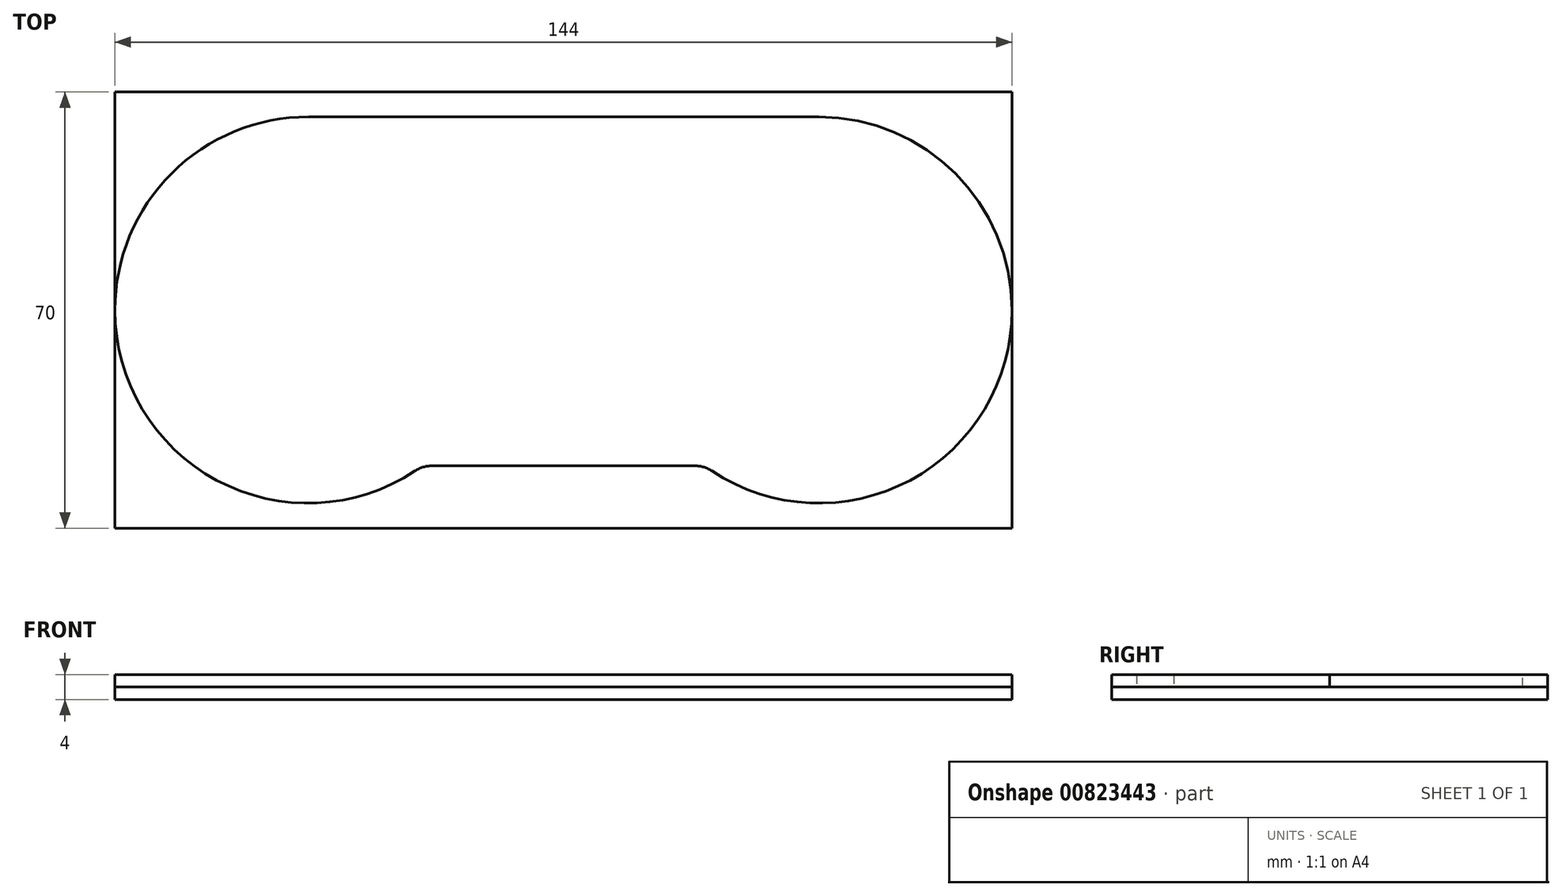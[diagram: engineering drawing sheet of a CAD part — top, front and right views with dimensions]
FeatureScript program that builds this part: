
annotation { "Feature Type Name" : "Feature", "Feature Type Description" : "" }
export const myFeature = defineFeature(function(context is Context, id is Id, definition is map)
    precondition{}
    {
        {
            var Q0;
            Q0=qCreatedBy(makeId("Top.planeOp"),FACE);
            var sketch = newSketch(context, id + "F0", { "sketchPlane" : qUnion([Q0])});
            skLineSegment(sketch, "E0.bottom", {"start": v(72, 35) * mm, "end": v(-72, 35) * mm});
            skLineSegment(sketch, "E0.top", {"start": v(72, -35) * mm, "end": v(-72, -35) * mm});
            skLineSegment(sketch, "E0.left", {"start": v(72, 35) * mm, "end": v(72, -35) * mm});
            skLineSegment(sketch, "E0.right", {"start": v(-72, 35) * mm, "end": v(-72, -35) * mm});
            skPoint(sketch, "E0.middle", {"position": v(0, 0) * mm});
            skArc(sketch, "E1", {"start": v(-40.92, 31) * mm, "mid": v(-70.7, -8.91) * mm, "end": v(-23.86, -25.83) * mm});
            skArc(sketch, "E2", {"start": v(23.86, -25.83) * mm, "mid": v(70.68, -8.95) * mm, "end": v(41, 31) * mm});
            skLineSegment(sketch, "E3", {"start": v(-40.92, 31) * mm, "end": v(41, 31) * mm});
            skPoint(sketch, "E4.visualSharp", {"position": v(-20.14, -22.93) * mm});
            skPoint(sketch, "E5.visualSharp", {"position": v(20.15, -22.94) * mm});
            skLineSegment(sketch, "E6.0", {"start": v(21.1, -25) * mm, "end": v(-21.1, -25) * mm});
            skPoint(sketch, "E7.start.orphan", {"position": v(41, -31) * mm});
            skPoint(sketch, "E8.visualSharp", {"position": v(22.67, -25) * mm});
            skArc(sketch, "E8.filletArc", {"start": v(23.86, -25.83) * mm, "mid": v(22.54, -25.21) * mm, "end": v(21.1, -25) * mm});
            skPoint(sketch, "E9.visualSharp", {"position": v(-22.67, -25) * mm});
            skArc(sketch, "E9.filletArc", {"start": v(-21.1, -25) * mm, "mid": v(-22.54, -25.21) * mm, "end": v(-23.86, -25.83) * mm});
            skSolve(sketch);
        }
        {
            var Q0;
            {var subQ4=sQuery(id+"F0.wireOp",EDGE,"E0.top");Q0=makeQuery(id+"F0.imprint","IMPRINT",FACE,{"disambiguationData":[TD([[makeQuery(id+"F0.imprint","IMPRINT",EDGE,{"derivedFrom":subQ4}),-1.0]])]});}
            var Q1;
            {var subQ4=sQuery(id+"F0.wireOp",EDGE,"E0.bottom");Q1=makeQuery(id+"F0.imprint","IMPRINT",FACE,{"disambiguationData":[TD([[makeQuery(id+"F0.imprint","IMPRINT",EDGE,{"derivedFrom":subQ4}),1.0]])]});}
            extrude(context, id + "F1", {"entities" : qUnion([Q0, Q1]), "depth" : 2 * mm, "offsetDistance" : 25 * mm});
        }
        {
            var Q0;
            {var subQ0=sQuery(id+"F0.wireOp",EDGE,"E3");Q0=makeQuery(id+"F0.imprint","IMPRINT",FACE,{"disambiguationData":[TD([[makeQuery(id+"F0.imprint","IMPRINT",EDGE,{"derivedFrom":subQ0}),-1.0]])]});}
            var Q1;
            Q1=makeQuery(id+"F1.opExtrude","CAP_FACE",FACE,{"disambiguationData":[OSD([sQuery(id+"F0.wireOp",EDGE,"E0.bottom"),sQuery(id+"F0.wireOp",EDGE,"E0.left"),sQuery(id+"F0.wireOp",EDGE,"E0.right"),sQuery(id+"F0.wireOp",EDGE,"E1"),sQuery(id+"F0.wireOp",EDGE,"E2"),sQuery(id+"F0.wireOp",EDGE,"E3")])],"isStart":false});
            var Q2;
            Q2=makeQuery(id+"F1.opExtrude","CAP_FACE",FACE,{"disambiguationData":[OSD([sQuery(id+"F0.wireOp",EDGE,"E0.top"),sQuery(id+"F0.wireOp",EDGE,"E0.left"),sQuery(id+"F0.wireOp",EDGE,"E0.right"),sQuery(id+"F0.wireOp",EDGE,"E1"),sQuery(id+"F0.wireOp",EDGE,"E2"),sQuery(id+"F0.wireOp",EDGE,"E6.0"),sQuery(id+"F0.wireOp",EDGE,"E8.filletArc"),sQuery(id+"F0.wireOp",EDGE,"E9.filletArc")])],"isStart":false});
            var Q3;
            {var subQ4=sQuery(id+"F0.wireOp",EDGE,"E0.top");Q3=makeQuery(id+"F0.imprint","IMPRINT",FACE,{"disambiguationData":[TD([[makeQuery(id+"F0.imprint","IMPRINT",EDGE,{"derivedFrom":subQ4}),-1.0]])]});}
            var Q4;
            {var subQ4=sQuery(id+"F0.wireOp",EDGE,"E0.bottom");Q4=makeQuery(id+"F0.imprint","IMPRINT",FACE,{"disambiguationData":[TD([[makeQuery(id+"F0.imprint","IMPRINT",EDGE,{"derivedFrom":subQ4}),1.0]])]});}
            extrude(context, id + "F2", {"entities" : qUnion([Q0, Q1, Q2, Q3, Q4]), "depth" : -2 * mm, "offsetDistance" : 25 * mm});
        }
    });
